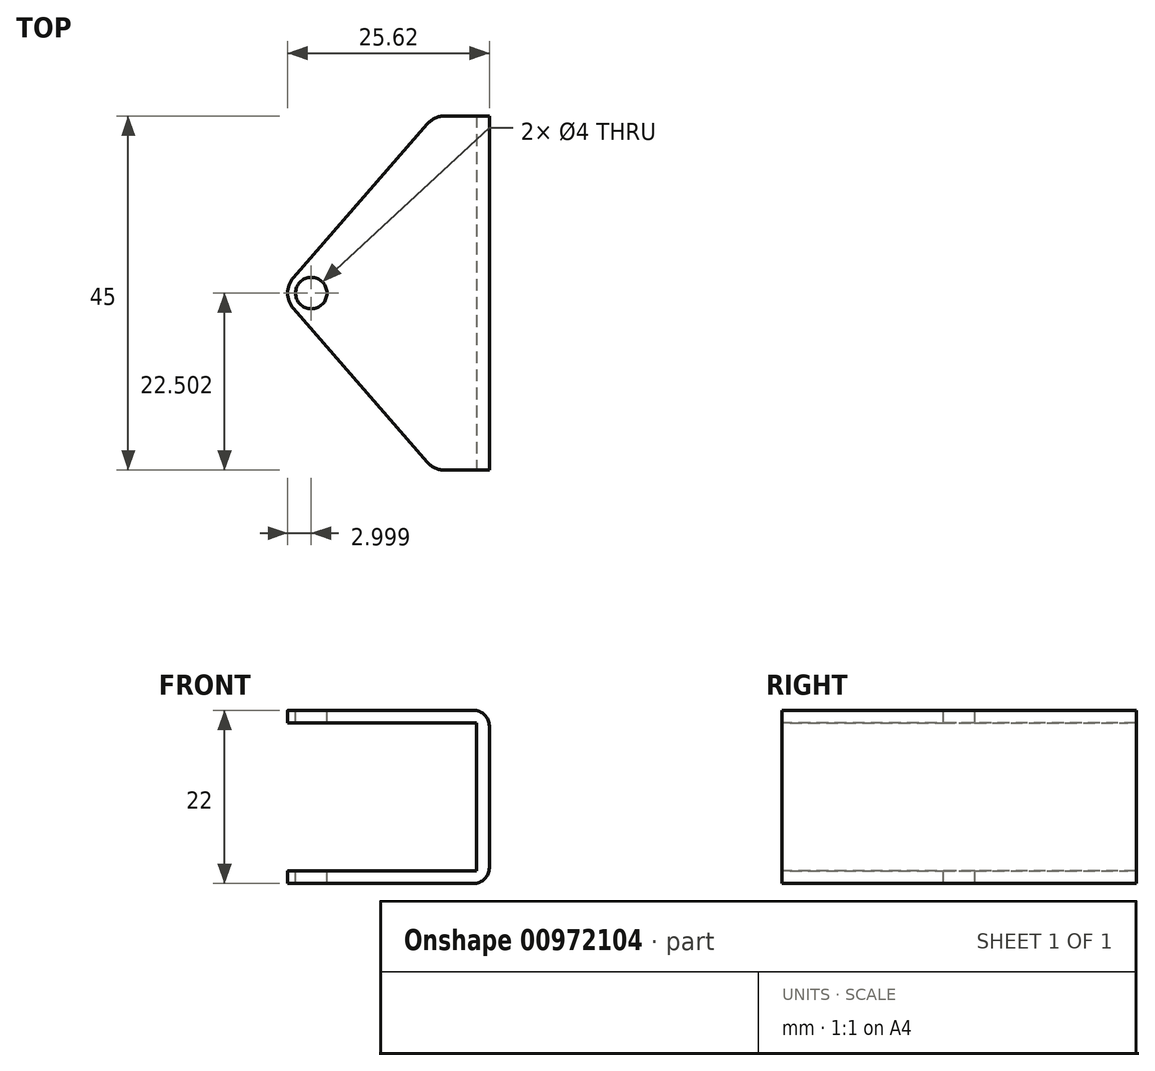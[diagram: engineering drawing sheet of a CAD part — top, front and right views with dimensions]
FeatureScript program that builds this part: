
annotation { "Feature Type Name" : "Feature", "Feature Type Description" : "" }
export const myFeature = defineFeature(function(context is Context, id is Id, definition is map)
    precondition{}
    {
        {
            var Q0;
            Q0=qCreatedBy(makeId("Right.planeOp"),FACE);
            var sketch = newSketch(context, id + "F0", { "sketchPlane" : qUnion([Q0])});
            skLineSegment(sketch, "E0.bottom", {"start": v(-18.6, 10.37) * mm, "end": v(26.4, 10.37) * mm});
            skLineSegment(sketch, "E0.top", {"start": v(-18.6, -11.63) * mm, "end": v(26.4, -11.63) * mm});
            skLineSegment(sketch, "E0.left", {"start": v(-18.6, 10.37) * mm, "end": v(-18.6, -11.63) * mm});
            skLineSegment(sketch, "E0.right", {"start": v(26.4, 10.37) * mm, "end": v(26.4, -11.63) * mm});
            skSolve(sketch);
        }
        {
            var Q0;
            Q0=makeQuery(id+"F0.imprint","IMPRINT",FACE,{"disambiguationData":[TD([[makeQuery(id+"F0.imprint","IMPRINT",EDGE,{"derivedFrom":sQuery(id+"F0.wireOp",EDGE,"E0.bottom")}),-1.0]])]});
            extrude(context, id + "F1", {"entities" : qUnion([Q0]), "depth" : 1.6 * mm, "offsetDistance" : 25 * mm});
        }
        {
            var Q0;
            Q0=makeQuery(id+"F1.opExtrude","CAP_FACE",FACE,{"disambiguationData":[OSD([sQuery(id+"F0.wireOp",EDGE,"E0.bottom"),sQuery(id+"F0.wireOp",EDGE,"E0.top"),sQuery(id+"F0.wireOp",EDGE,"E0.left"),sQuery(id+"F0.wireOp",EDGE,"E0.right")])],"isStart":true});
            var sketch = newSketch(context, id + "F2", { "sketchPlane" : qUnion([Q0])});
            skLineSegment(sketch, "E1.bottom", {"start": v(-26.4, 10.37) * mm, "end": v(18.6, 10.37) * mm});
            skLineSegment(sketch, "E1.top", {"start": v(-26.4, 8.77) * mm, "end": v(18.6, 8.77) * mm});
            skLineSegment(sketch, "E1.left", {"start": v(-26.4, 10.37) * mm, "end": v(-26.4, 8.77) * mm});
            skLineSegment(sketch, "E1.right", {"start": v(18.6, 10.37) * mm, "end": v(18.6, 8.77) * mm});
            skLineSegment(sketch, "E2.bottom", {"start": v(-26.4, -11.63) * mm, "end": v(18.6, -11.63) * mm});
            skLineSegment(sketch, "E2.top", {"start": v(-26.4, -10.03) * mm, "end": v(18.6, -10.03) * mm});
            skLineSegment(sketch, "E2.left", {"start": v(-26.4, -11.63) * mm, "end": v(-26.4, -10.03) * mm});
            skLineSegment(sketch, "E2.right", {"start": v(18.6, -11.63) * mm, "end": v(18.6, -10.03) * mm});
            skSolve(sketch);
        }
        {
            var Q0;
            Q0=makeQuery(id+"F2.imprint","IMPRINT",FACE,{"disambiguationData":[TD([[makeQuery(id+"F2.imprint","IMPRINT",EDGE,{"derivedFrom":sQuery(id+"F2.wireOp",EDGE,"E1.bottom")}),1.0]])]});
            var Q1;
            Q1=makeQuery(id+"F2.imprint","IMPRINT",FACE,{"disambiguationData":[TD([[makeQuery(id+"F2.imprint","IMPRINT",EDGE,{"derivedFrom":sQuery(id+"F2.wireOp",EDGE,"E2.bottom")}),-1.0]])]});
            extrude(context, id + "F3", {"entities" : qUnion([Q0, Q1]), "operationType" : NewBodyOperationType.ADD, "depth" : 25 * mm, "offsetDistance" : 25 * mm});
        }
        {
            var Q0;
            Q0=makeQuery(id+"F3.boolean.opBoolean","MERGE",FACE,{"derivedFrom":[makeQuery(id+"F1.opExtrude","SWEPT_FACE",FACE,{"disambiguationData":[OSD([sQuery(id+"F0.wireOp",EDGE,"E0.bottom")])]}),makeQuery(id+"F3.opExtrude","SWEPT_FACE",FACE,{"disambiguationData":[OSD([sQuery(id+"F2.wireOp",EDGE,"E1.bottom")])]})]});
            var sketch = newSketch(context, id + "F4", { "sketchPlane" : qUnion([Q0])});
            skLineSegment(sketch, "E3", {"start": v(1.6, -18.6) * mm, "end": v(-4.03, -18.6) * mm});
            skLineSegment(sketch, "E4", {"start": v(-6.3, -17.57) * mm, "end": v(-23.28, 1.93) * mm});
            skLineSegment(sketch, "E5", {"start": v(-23.28, 5.87) * mm, "end": v(-6.3, 25.37) * mm});
            skLineSegment(sketch, "E6", {"start": v(-4.03, 26.4) * mm, "end": v(1.6, 26.4) * mm});
            skPoint(sketch, "E7.visualSharp", {"position": v(-25, 3.9) * mm});
            skArc(sketch, "E7.filletArc", {"start": v(-23.28, 5.87) * mm, "mid": v(-24.02, 3.9) * mm, "end": v(-23.28, 1.93) * mm});
            skPoint(sketch, "E8.visualSharp", {"position": v(-5.4, -18.6) * mm});
            skArc(sketch, "E8.filletArc", {"start": v(-6.3, -17.57) * mm, "mid": v(-5.28, -18.33) * mm, "end": v(-4.03, -18.6) * mm});
            skPoint(sketch, "E9.visualSharp", {"position": v(-5.4, 26.4) * mm});
            skArc(sketch, "E9.filletArc", {"start": v(-4.03, 26.4) * mm, "mid": v(-5.28, 26.13) * mm, "end": v(-6.3, 25.37) * mm});
            skCircle(sketch, "E10", {"center": v(-21.02, 3.9) * mm, "radius": 2 * mm});
            skLineSegment(sketch, "E11", {"start": v(-4.03, 26.4) * mm, "end": v(-25, 26.4) * mm});
            skLineSegment(sketch, "E12", {"start": v(-25, 26.4) * mm, "end": v(-25, -18.6) * mm});
            skLineSegment(sketch, "E13", {"start": v(-25, -18.6) * mm, "end": v(-4.03, -18.6) * mm});
            skSolve(sketch);
        }
        {
            var Q0;
            Q0=makeQuery(id+"F4.imprint","IMPRINT",FACE,{"disambiguationData":[TD([[makeQuery(id+"F4.imprint","IMPRINT",EDGE,{"derivedFrom":sQuery(id+"F4.wireOp",EDGE,"E4")}),1.0]])]});
            var Q1;
            Q1=makeQuery(id+"F4.imprint","IMPRINT",FACE,{"disambiguationData":[TD([[makeQuery(id+"F4.imprint","IMPRINT",EDGE,{"derivedFrom":sQuery(id+"F4.wireOp",EDGE,"E10")}),1.0]])]});
            extrude(context, id + "F5", {"entities" : qUnion([Q0, Q1]), "operationType" : NewBodyOperationType.REMOVE, "oppositeDirection" : true, "depth" : 25 * mm, "offsetDistance" : 25 * mm});
        }
        {
            var Q0;
            Q0=makeQuery(id+"F1.opExtrude","CAP_EDGE",EDGE,{"disambiguationData":[OSD([sQuery(id+"F0.wireOp",EDGE,"E0.top")])],"isStart":false});
            var Q1;
            Q1=makeQuery(id+"F1.opExtrude","CAP_EDGE",EDGE,{"disambiguationData":[OSD([sQuery(id+"F0.wireOp",EDGE,"E0.bottom")])],"isStart":false});
            var Q2;
            Q2=makeQuery(id+"F3.opExtrude","CAP_EDGE",EDGE,{"disambiguationData":[OSD([sQuery(id+"F2.wireOp",EDGE,"E2.top")])],"isStart":true});
            var Q3;
            Q3=makeQuery(id+"F3.opExtrude","CAP_EDGE",EDGE,{"disambiguationData":[OSD([sQuery(id+"F2.wireOp",EDGE,"E1.top")])],"isStart":true});
            fillet(context, id + "F6", {"entities" : qUnion([Q0, Q1, Q2, Q3]), "radius" : 2 * mm, "tangentPropagation" : true, "allowEdgeOverflow" : false});
        }
    });
